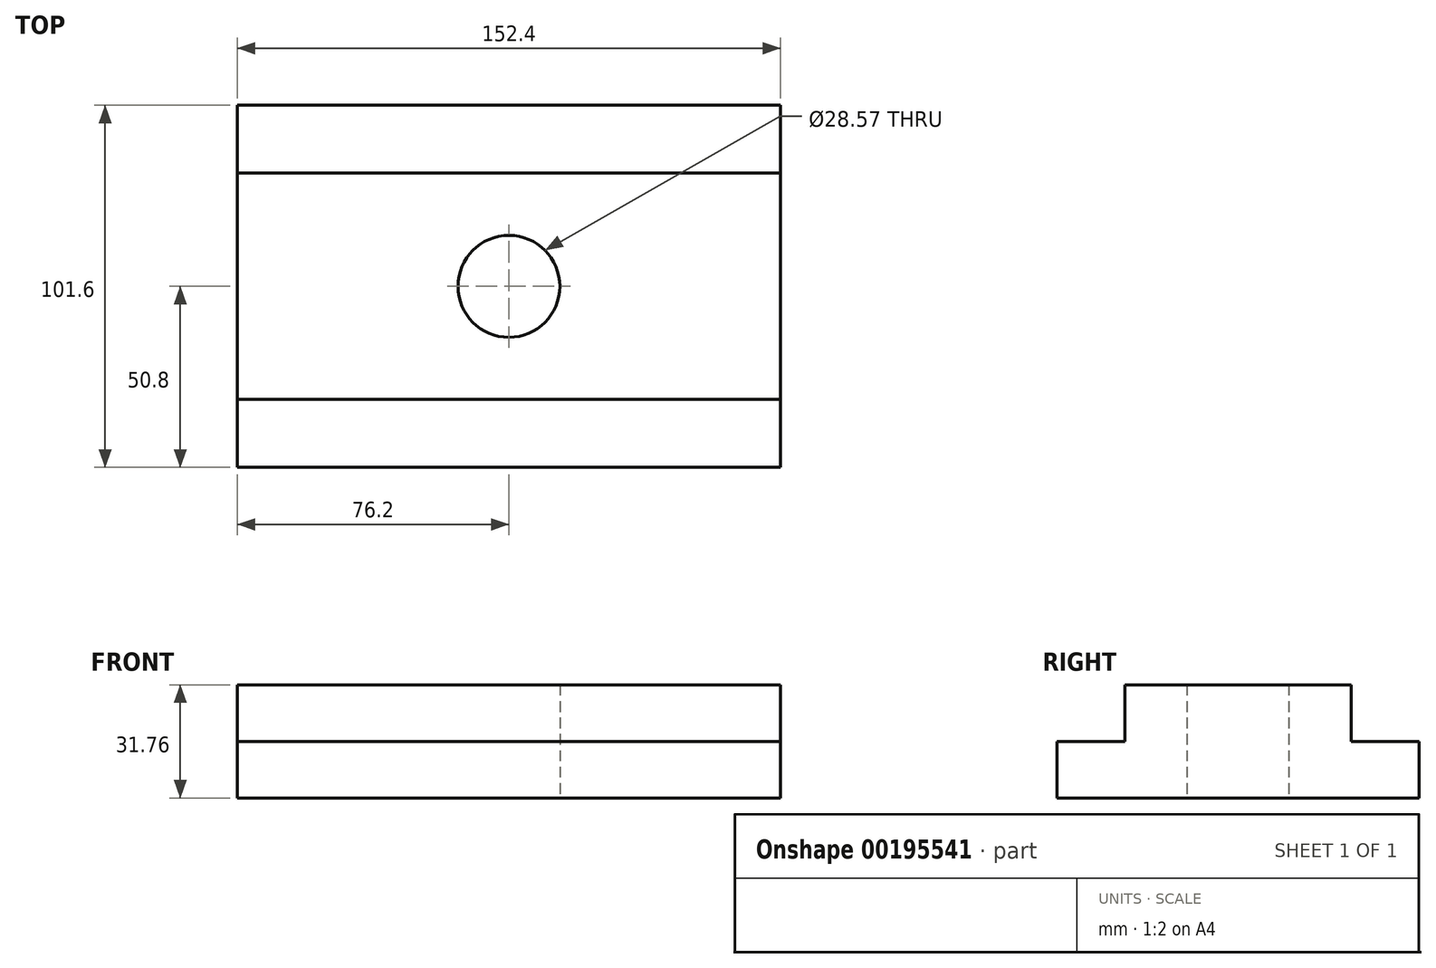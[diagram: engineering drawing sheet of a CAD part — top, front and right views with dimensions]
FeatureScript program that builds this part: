
annotation { "Feature Type Name" : "Feature", "Feature Type Description" : "" }
export const myFeature = defineFeature(function(context is Context, id is Id, definition is map)
    precondition{}
    {
        {
            var Q0;
            Q0=qCreatedBy(makeId("Top.planeOp"),FACE);
            var sketch = newSketch(context, id + "F0", { "sketchPlane" : qUnion([Q0])});
            skPoint(sketch, "E0.middle", {"position": v(0, 0) * mm});
            skPoint(sketch, "E0.left.end.orphan", {"position": v(116.87, 50.8) * mm});
            skPoint(sketch, "E0.bottom.start.orphan", {"position": v(76.2, -50.8) * mm});
            skPoint(sketch, "E0.right.end.orphan", {"position": v(-76.2, 50.8) * mm});
            skPoint(sketch, "E0.right.start.orphan", {"position": v(-116.87, -50.8) * mm});
            skLineSegment(sketch, "E1.bottom", {"start": v(-76.2, 50.8) * mm, "end": v(76.2, 50.8) * mm});
            skLineSegment(sketch, "E1.top", {"start": v(-76.2, -50.8) * mm, "end": v(76.2, -50.8) * mm});
            skLineSegment(sketch, "E1.left", {"start": v(-76.2, 50.8) * mm, "end": v(-76.2, -50.8) * mm});
            skLineSegment(sketch, "E1.right", {"start": v(76.2, 50.8) * mm, "end": v(76.2, -50.8) * mm});
            skPoint(sketch, "E2.right.end.orphan", {"position": v(-76.2, 31.75) * mm});
            skPoint(sketch, "E2.right.start.orphan", {"position": v(-76.2, -31.75) * mm});
            skPoint(sketch, "E2.left.end.orphan", {"position": v(76.2, 31.75) * mm});
            skPoint(sketch, "E2.left.start.orphan", {"position": v(76.2, -31.75) * mm});
            skLineSegment(sketch, "E3", {"start": v(-76.2, 31.75) * mm, "end": v(76.2, 31.75) * mm});
            skLineSegment(sketch, "E4", {"start": v(0, 0) * mm, "end": v(76.2, 0) * mm});
            skLineSegment(sketch, "E5.MirrorCS", {"start": v(-76.2, -31.75) * mm, "end": v(76.2, -31.75) * mm});
            skCircle(sketch, "E6", {"center": v(0, 0) * mm, "radius": 14.29 * mm});
            skSolve(sketch);
        }
        {
            var Q0;
            {var subQ0=sQuery(id+"F0.wireOp",EDGE,"E3");Q0=makeQuery(id+"F0.imprint","IMPRINT",FACE,{"disambiguationData":[TD([[makeQuery(id+"F0.imprint","IMPRINT",EDGE,{"derivedFrom":subQ0}),-1.0]])]});}
            extrude(context, id + "F1", {"entities" : qUnion([Q0]), "depth" : 15.88 * mm});
        }
        {
            var Q0;
            {var subQ0=sQuery(id+"F0.wireOp",EDGE,"E1.bottom");Q0=makeQuery(id+"F0.imprint","IMPRINT",FACE,{"disambiguationData":[TD([[makeQuery(id+"F0.imprint","IMPRINT",EDGE,{"derivedFrom":subQ0}),-1.0]])]});}
            var Q1;
            {var subQ0=sQuery(id+"F0.wireOp",EDGE,"E3");Q1=makeQuery(id+"F0.imprint","IMPRINT",FACE,{"disambiguationData":[TD([[makeQuery(id+"F0.imprint","IMPRINT",EDGE,{"derivedFrom":subQ0}),-1.0]])]});}
            var Q2;
            {var subQ0=sQuery(id+"F0.wireOp",EDGE,"E1.top");Q2=makeQuery(id+"F0.imprint","IMPRINT",FACE,{"disambiguationData":[TD([[makeQuery(id+"F0.imprint","IMPRINT",EDGE,{"derivedFrom":subQ0}),1.0]])]});}
            extrude(context, id + "F2", {"entities" : qUnion([Q0, Q1, Q2]), "operationType" : NewBodyOperationType.ADD, "oppositeDirection" : true, "depth" : 15.88 * mm});
        }
    });
